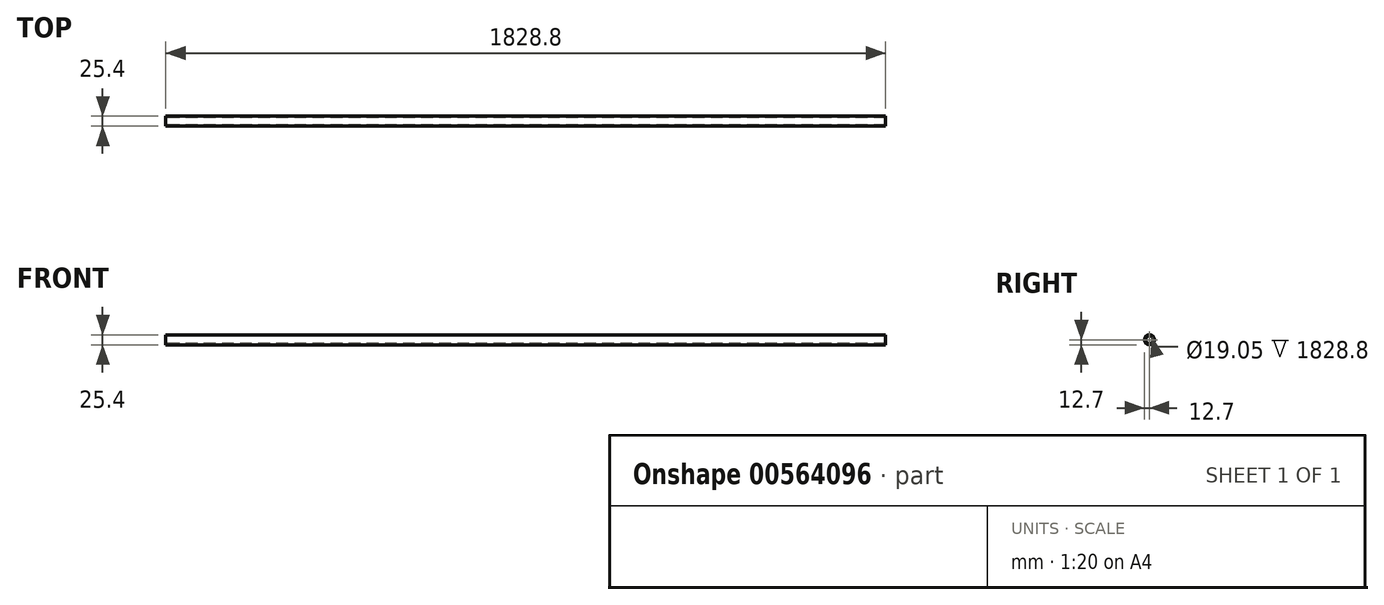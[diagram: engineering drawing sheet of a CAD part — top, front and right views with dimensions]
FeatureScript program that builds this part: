
annotation { "Feature Type Name" : "Feature", "Feature Type Description" : "" }
export const myFeature = defineFeature(function(context is Context, id is Id, definition is map)
    precondition{}
    {
        {
            var Q0;
            Q0=qCreatedBy(makeId("Right.planeOp"),FACE);
            var sketch = newSketch(context, id + "F0", { "sketchPlane" : qUnion([Q0])});
            skCircle(sketch, "E0", {"center": v(0, 0) * mm, "radius": 12.7 * mm});
            skCircle(sketch, "E1", {"center": v(0, 0) * mm, "radius": 9.53 * mm});
            skSolve(sketch);
        }
        {
            var Q0;
            Q0=makeQuery(id+"F0.imprint","IMPRINT",FACE,{"disambiguationData":[TD([[makeQuery(id+"F0.imprint","IMPRINT",EDGE,{"derivedFrom":sQuery(id+"F0.wireOp",EDGE,"E0")}),1.0]])]});
            extrude(context, id + "F1", {"entities" : qUnion([Q0]), "depth" : 1828.8 * mm, "offsetDistance" : 25.4 * mm});
        }
    });
